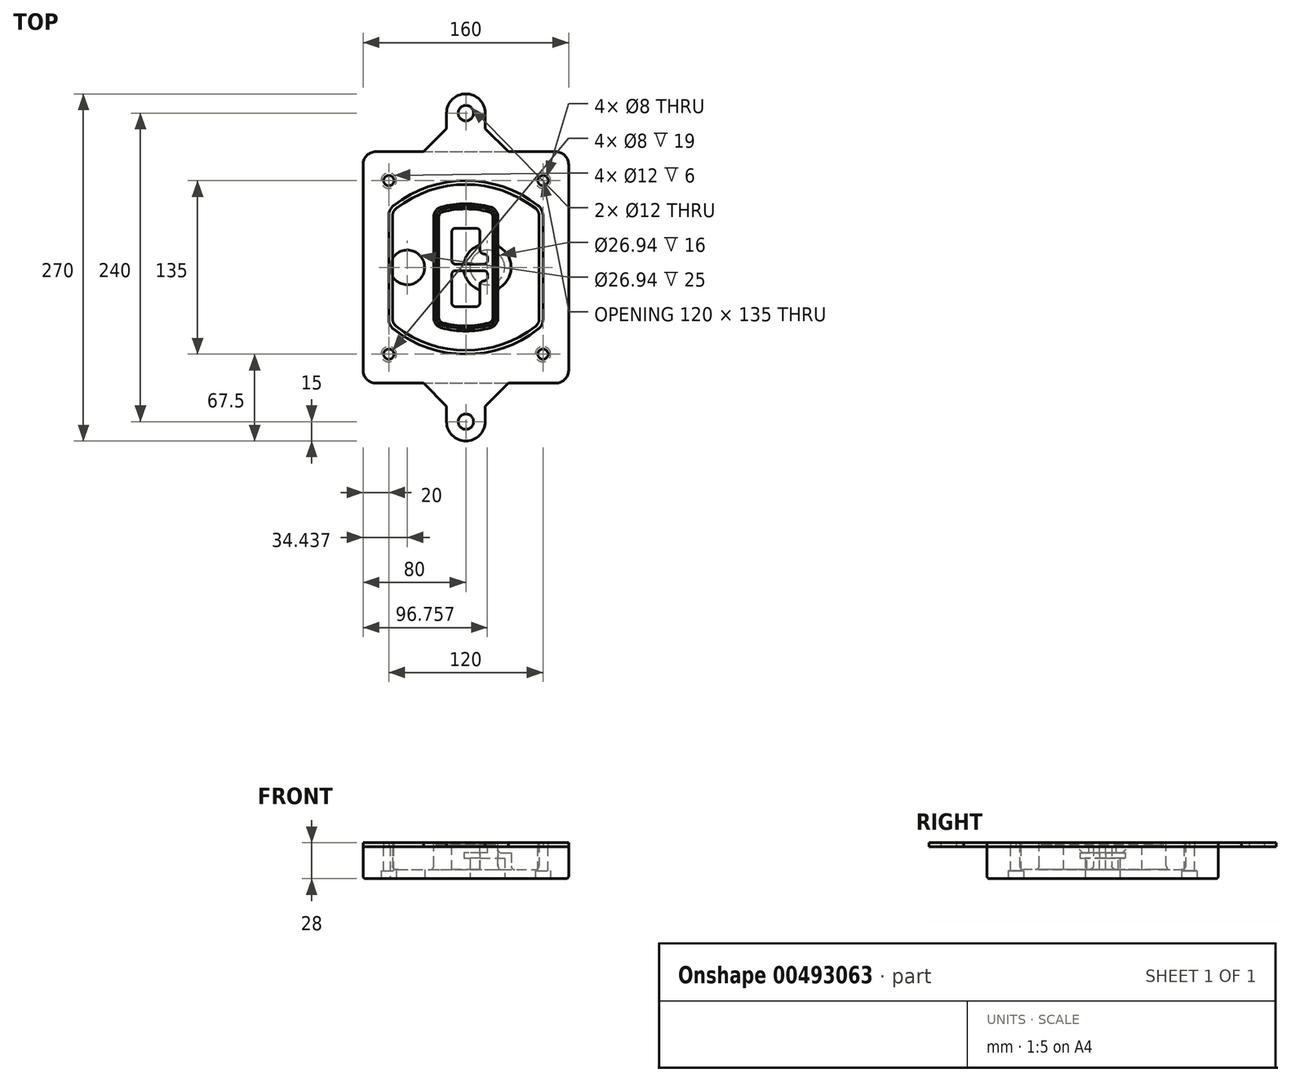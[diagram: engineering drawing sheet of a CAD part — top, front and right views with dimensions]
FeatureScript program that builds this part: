
annotation { "Feature Type Name" : "Feature", "Feature Type Description" : "" }
export const myFeature = defineFeature(function(context is Context, id is Id, definition is map)
    precondition{}
    {
        {
            var Q0;
            Q0=qCreatedBy(makeId("Top.planeOp"),FACE);
            var sketch = newSketch(context, id + "F0", { "sketchPlane" : qUnion([Q0])});
            skPoint(sketch, "E0.rect.middle", {"position": v(0, 0) * mm});
            skLineSegment(sketch, "E1.bottom", {"start": v(-70, -90) * mm, "end": v(70, -90) * mm});
            skLineSegment(sketch, "E1.top", {"start": v(-70, 90) * mm, "end": v(70, 90) * mm});
            skLineSegment(sketch, "E1.left", {"start": v(-80, -80) * mm, "end": v(-80, 80) * mm});
            skLineSegment(sketch, "E1.right", {"start": v(80, -80) * mm, "end": v(80, 80) * mm});
            skLineSegment(sketch, "E2", {"start": v(-80, 90) * mm, "end": v(80, -90) * mm, "construction": true});
            skLineSegment(sketch, "E3", {"start": v(80, 90) * mm, "end": v(-80, -90) * mm, "construction": true});
            skCircle(sketch, "E4", {"center": v(-60, 67.5) * mm, "radius": 4 * mm});
            skCircle(sketch, "E5", {"center": v(60, 67.5) * mm, "radius": 4 * mm});
            skCircle(sketch, "E6", {"center": v(60, -67.5) * mm, "radius": 4 * mm});
            skCircle(sketch, "E7", {"center": v(-60, -67.5) * mm, "radius": 4 * mm});
            skLineSegment(sketch, "E8", {"start": v(-60, 67.5) * mm, "end": v(60, 67.5) * mm, "construction": true});
            skLineSegment(sketch, "E9", {"start": v(60, 67.5) * mm, "end": v(60, -67.5) * mm, "construction": true});
            skLineSegment(sketch, "E10", {"start": v(60, -67.5) * mm, "end": v(-60, -67.5) * mm, "construction": true});
            skLineSegment(sketch, "E11", {"start": v(-60, -67.5) * mm, "end": v(-60, 67.5) * mm, "construction": true});
            skLineSegment(sketch, "E12", {"start": v(-60, 40.3) * mm, "end": v(-60, -40.3) * mm});
            skLineSegment(sketch, "E13", {"start": v(60, 40.3) * mm, "end": v(60, -40.3) * mm});
            skArc(sketch, "E14", {"start": v(56.15, 48.18) * mm, "mid": v(0, 67.5) * mm, "end": v(-56.15, 48.18) * mm});
            skArc(sketch, "E15", {"start": v(-56.15, -48.18) * mm, "mid": v(0, -67.5) * mm, "end": v(56.15, -48.18) * mm});
            skLineSegment(sketch, "E16", {"start": v(-60, 0) * mm, "end": v(60, 0) * mm, "construction": true});
            skPoint(sketch, "E17.visualSharp", {"position": v(-60, -45) * mm});
            skArc(sketch, "E17.filletArc", {"start": v(-60, -40.3) * mm, "mid": v(-58.99, -44.68) * mm, "end": v(-56.15, -48.18) * mm});
            skPoint(sketch, "E18.visualSharp", {"position": v(-60, 45) * mm});
            skArc(sketch, "E18.filletArc", {"start": v(-56.15, 48.18) * mm, "mid": v(-58.99, 44.68) * mm, "end": v(-60, 40.3) * mm});
            skPoint(sketch, "E19.visualSharp", {"position": v(60, 45) * mm});
            skArc(sketch, "E19.filletArc", {"start": v(60, 40.3) * mm, "mid": v(58.99, 44.68) * mm, "end": v(56.15, 48.18) * mm});
            skPoint(sketch, "E20.visualSharp", {"position": v(60, -45) * mm});
            skArc(sketch, "E20.filletArc", {"start": v(56.15, -48.18) * mm, "mid": v(58.99, -44.68) * mm, "end": v(60, -40.3) * mm});
            skPoint(sketch, "E21.visualSharp", {"position": v(-80, 90) * mm});
            skArc(sketch, "E21.filletArc", {"start": v(-70, 90) * mm, "mid": v(-77.07, 87.07) * mm, "end": v(-80, 80) * mm});
            skPoint(sketch, "E22.visualSharp", {"position": v(80, 90) * mm});
            skArc(sketch, "E22.filletArc", {"start": v(80, 80) * mm, "mid": v(77.07, 87.07) * mm, "end": v(70, 90) * mm});
            skPoint(sketch, "E23.visualSharp", {"position": v(80, -90) * mm});
            skArc(sketch, "E23.filletArc", {"start": v(70, -90) * mm, "mid": v(77.07, -87.07) * mm, "end": v(80, -80) * mm});
            skPoint(sketch, "E24.visualSharp", {"position": v(-80, -90) * mm});
            skArc(sketch, "E24.filletArc", {"start": v(-80, -80) * mm, "mid": v(-77.07, -87.07) * mm, "end": v(-70, -90) * mm});
            skArc(sketch, "E25.0", {"start": v(57, 40.3) * mm, "mid": v(56.3, 43.36) * mm, "end": v(54.3, 45.81) * mm});
            skLineSegment(sketch, "E25.1", {"start": v(57, 40.3) * mm, "end": v(57, -40.3) * mm});
            skArc(sketch, "E25.2", {"start": v(54.3, -45.81) * mm, "mid": v(56.3, -43.36) * mm, "end": v(57, -40.3) * mm});
            skArc(sketch, "E25.3", {"start": v(-54.3, -45.81) * mm, "mid": v(0, -64.5) * mm, "end": v(54.3, -45.81) * mm});
            skArc(sketch, "E25.4", {"start": v(-57, -40.3) * mm, "mid": v(-56.3, -43.36) * mm, "end": v(-54.3, -45.81) * mm});
            skArc(sketch, "E25.5", {"start": v(54.3, 45.81) * mm, "mid": v(0, 64.5) * mm, "end": v(-54.3, 45.81) * mm});
            skLineSegment(sketch, "E25.6", {"start": v(-57, 40.3) * mm, "end": v(-57, -40.3) * mm});
            skArc(sketch, "E25.7", {"start": v(-54.3, 45.81) * mm, "mid": v(-56.3, 43.36) * mm, "end": v(-57, 40.3) * mm});
            skArc(sketch, "E26.0", {"start": v(-58.62, 51.33) * mm, "mid": v(-62.58, 46.43) * mm, "end": v(-64, 40.3) * mm});
            skArc(sketch, "E26.1", {"start": v(58.62, 51.33) * mm, "mid": v(0, 71.5) * mm, "end": v(-58.62, 51.33) * mm});
            skArc(sketch, "E26.2", {"start": v(64, 40.3) * mm, "mid": v(62.58, 46.43) * mm, "end": v(58.62, 51.33) * mm});
            skLineSegment(sketch, "E26.3", {"start": v(64, 40.3) * mm, "end": v(64, -40.3) * mm});
            skArc(sketch, "E26.4", {"start": v(58.62, -51.33) * mm, "mid": v(62.58, -46.43) * mm, "end": v(64, -40.3) * mm});
            skLineSegment(sketch, "E26.5", {"start": v(-64, 40.3) * mm, "end": v(-64, -40.3) * mm});
            skArc(sketch, "E26.6", {"start": v(-58.62, -51.33) * mm, "mid": v(0, -71.5) * mm, "end": v(58.62, -51.33) * mm});
            skArc(sketch, "E26.7", {"start": v(-64, -40.3) * mm, "mid": v(-62.58, -46.43) * mm, "end": v(-58.62, -51.33) * mm});
            skSolve(sketch);
        }
        {
            var Q0;
            Q0=makeQuery(id+"F0.imprint","IMPRINT",FACE,{"disambiguationData":[TD([[makeQuery(id+"F0.imprint","IMPRINT",EDGE,{"derivedFrom":sQuery(id+"F0.wireOp",EDGE,"E1.bottom")}),1.0]])]});
            var Q1;
            Q1=makeQuery(id+"F0.imprint","IMPRINT",FACE,{"disambiguationData":[TD([[makeQuery(id+"F0.imprint","IMPRINT",EDGE,{"derivedFrom":sQuery(id+"F0.wireOp",EDGE,"E12")}),1.0]])]});
            var Q2;
            Q2=makeQuery(id+"F0.imprint","IMPRINT",FACE,{"disambiguationData":[TD([[makeQuery(id+"F0.imprint","IMPRINT",EDGE,{"derivedFrom":sQuery(id+"F0.wireOp",EDGE,"E25.0")}),1.0]])]});
            var Q3;
            Q3=makeQuery(id+"F0.imprint","IMPRINT",FACE,{"disambiguationData":[TD([[makeQuery(id+"F0.imprint","IMPRINT",EDGE,{"derivedFrom":sQuery(id+"F0.wireOp",EDGE,"E12")}),-1.0]])]});
            extrude(context, id + "F1", {"entities" : qUnion([Q0, Q1, Q2, Q3]), "oppositeDirection" : true, "depth" : 25 * mm});
        }
        {
            var Q0;
            Q0=makeQuery(id+"F0.imprint","IMPRINT",FACE,{"disambiguationData":[TD([[makeQuery(id+"F0.imprint","IMPRINT",EDGE,{"derivedFrom":sQuery(id+"F0.wireOp",EDGE,"E12")}),1.0]])]});
            extrude(context, id + "F2", {"entities" : qUnion([Q0]), "operationType" : NewBodyOperationType.ADD, "depth" : 3 * mm});
        }
        {
            var Q0;
            Q0=makeQuery(id+"F0.imprint","IMPRINT",FACE,{"disambiguationData":[TD([[makeQuery(id+"F0.imprint","IMPRINT",EDGE,{"derivedFrom":sQuery(id+"F0.wireOp",EDGE,"E25.0")}),1.0]])]});
            extrude(context, id + "F3", {"entities" : qUnion([Q0]), "operationType" : NewBodyOperationType.REMOVE, "oppositeDirection" : true, "depth" : 18 * mm});
        }
        {
            var Q0;
            Q0=makeQuery(id+"F2.opExtrude","CAP_FACE",FACE,{"disambiguationData":[OSD([sQuery(id+"F0.wireOp",EDGE,"E12"),sQuery(id+"F0.wireOp",EDGE,"E13"),sQuery(id+"F0.wireOp",EDGE,"E14"),sQuery(id+"F0.wireOp",EDGE,"E15"),sQuery(id+"F0.wireOp",EDGE,"E17.filletArc"),sQuery(id+"F0.wireOp",EDGE,"E18.filletArc"),sQuery(id+"F0.wireOp",EDGE,"E19.filletArc"),sQuery(id+"F0.wireOp",EDGE,"E20.filletArc"),sQuery(id+"F0.wireOp",EDGE,"E25.0"),sQuery(id+"F0.wireOp",EDGE,"E25.1"),sQuery(id+"F0.wireOp",EDGE,"E25.2"),sQuery(id+"F0.wireOp",EDGE,"E25.3"),sQuery(id+"F0.wireOp",EDGE,"E25.4"),sQuery(id+"F0.wireOp",EDGE,"E25.5"),sQuery(id+"F0.wireOp",EDGE,"E25.6"),sQuery(id+"F0.wireOp",EDGE,"E25.7")])],"isStart":false});
            var sketch = newSketch(context, id + "F4", { "sketchPlane" : qUnion([Q0])});
            skArc(sketch, "E27.0", {"start": v(-19.08, -46.97) * mm, "mid": v(0, -49.5) * mm, "end": v(19.08, -46.97) * mm});
            skArc(sketch, "E28.0", {"start": v(19.08, 46.97) * mm, "mid": v(0, 49.5) * mm, "end": v(-19.08, 46.97) * mm});
            skLineSegment(sketch, "E29", {"start": v(-25, 39.25) * mm, "end": v(-25, -39.25) * mm});
            skLineSegment(sketch, "E30", {"start": v(25, 39.25) * mm, "end": v(25, -39.25) * mm});
            skLineSegment(sketch, "E31", {"start": v(-25, 45.1) * mm, "end": v(25, 45.1) * mm, "construction": true});
            skLineSegment(sketch, "E32", {"start": v(-25, -45.1) * mm, "end": v(25, -45.1) * mm, "construction": true});
            skPoint(sketch, "E33.visualSharp", {"position": v(-25, 45.1) * mm});
            skArc(sketch, "E33.filletArc", {"start": v(-19.08, 46.97) * mm, "mid": v(-23.35, 44.11) * mm, "end": v(-25, 39.25) * mm});
            skPoint(sketch, "E34.visualSharp", {"position": v(25, 45.1) * mm});
            skArc(sketch, "E34.filletArc", {"start": v(25, 39.25) * mm, "mid": v(23.35, 44.11) * mm, "end": v(19.08, 46.97) * mm});
            skPoint(sketch, "E35.visualSharp", {"position": v(25, -45.1) * mm});
            skArc(sketch, "E35.filletArc", {"start": v(19.08, -46.97) * mm, "mid": v(23.35, -44.11) * mm, "end": v(25, -39.25) * mm});
            skPoint(sketch, "E36.visualSharp", {"position": v(-25, -45.1) * mm});
            skArc(sketch, "E36.filletArc", {"start": v(-25, -39.25) * mm, "mid": v(-23.35, -44.11) * mm, "end": v(-19.08, -46.97) * mm});
            skArc(sketch, "E37.0", {"start": v(54.3, 45.81) * mm, "mid": v(0, 64.5) * mm, "end": v(-54.3, 45.81) * mm});
            skArc(sketch, "E37.1", {"start": v(-54.3, 45.81) * mm, "mid": v(-56.3, 43.36) * mm, "end": v(-57, 40.3) * mm});
            skLineSegment(sketch, "E37.2", {"start": v(-57, 40.3) * mm, "end": v(-57, -40.3) * mm});
            skArc(sketch, "E37.3", {"start": v(-57, -40.3) * mm, "mid": v(-56.3, -43.36) * mm, "end": v(-54.3, -45.81) * mm});
            skArc(sketch, "E37.4", {"start": v(-54.3, -45.81) * mm, "mid": v(0, -64.5) * mm, "end": v(54.3, -45.81) * mm});
            skArc(sketch, "E37.5", {"start": v(54.3, -45.81) * mm, "mid": v(56.3, -43.36) * mm, "end": v(57, -40.3) * mm});
            skLineSegment(sketch, "E37.6", {"start": v(57, 40.3) * mm, "end": v(57, -40.3) * mm});
            skArc(sketch, "E37.7", {"start": v(57, 40.3) * mm, "mid": v(56.3, 43.36) * mm, "end": v(54.3, 45.81) * mm});
            skLineSegment(sketch, "E38.0", {"start": v(23, 39.25) * mm, "end": v(23, -39.25) * mm});
            skArc(sketch, "E38.1", {"start": v(18.56, -45.04) * mm, "mid": v(21.76, -42.9) * mm, "end": v(23, -39.25) * mm});
            skArc(sketch, "E38.2", {"start": v(-18.56, -45.04) * mm, "mid": v(0, -47.5) * mm, "end": v(18.56, -45.04) * mm});
            skArc(sketch, "E38.3", {"start": v(-23, -39.25) * mm, "mid": v(-21.76, -42.9) * mm, "end": v(-18.56, -45.04) * mm});
            skLineSegment(sketch, "E38.4", {"start": v(-23, 39.25) * mm, "end": v(-23, -39.25) * mm});
            skArc(sketch, "E38.5", {"start": v(23, 39.25) * mm, "mid": v(21.76, 42.9) * mm, "end": v(18.56, 45.04) * mm});
            skArc(sketch, "E38.6", {"start": v(-18.56, 45.04) * mm, "mid": v(-21.76, 42.9) * mm, "end": v(-23, 39.25) * mm});
            skArc(sketch, "E38.7", {"start": v(18.56, 45.04) * mm, "mid": v(0, 47.5) * mm, "end": v(-18.56, 45.04) * mm});
            skArc(sketch, "E39.0", {"start": v(21, 39.25) * mm, "mid": v(20.18, 41.68) * mm, "end": v(18.04, 43.1) * mm});
            skLineSegment(sketch, "E39.1", {"start": v(21, 39.25) * mm, "end": v(21, -39.25) * mm});
            skArc(sketch, "E39.2", {"start": v(18.04, -43.1) * mm, "mid": v(20.18, -41.68) * mm, "end": v(21, -39.25) * mm});
            skArc(sketch, "E39.3", {"start": v(-18.04, -43.1) * mm, "mid": v(0, -45.5) * mm, "end": v(18.04, -43.1) * mm});
            skArc(sketch, "E39.4", {"start": v(-21, -39.25) * mm, "mid": v(-20.18, -41.68) * mm, "end": v(-18.04, -43.1) * mm});
            skArc(sketch, "E39.5", {"start": v(18.04, 43.1) * mm, "mid": v(0, 45.5) * mm, "end": v(-18.04, 43.1) * mm});
            skLineSegment(sketch, "E39.6", {"start": v(-21, 39.25) * mm, "end": v(-21, -39.25) * mm});
            skArc(sketch, "E39.7", {"start": v(-18.04, 43.1) * mm, "mid": v(-20.18, 41.68) * mm, "end": v(-21, 39.25) * mm});
            skLineSegment(sketch, "E40", {"start": v(-25, 0) * mm, "end": v(25, 0) * mm, "construction": true});
            skLineSegment(sketch, "E41", {"start": v(-11, 5.5) * mm, "end": v(-11, 27.5) * mm});
            skLineSegment(sketch, "E42", {"start": v(-8, 30.5) * mm, "end": v(8, 30.5) * mm});
            skLineSegment(sketch, "E43", {"start": v(11, 27.5) * mm, "end": v(11, 13.5) * mm});
            skLineSegment(sketch, "E44", {"start": v(14, 10.5) * mm, "end": v(14, 10.5) * mm});
            skLineSegment(sketch, "E45", {"start": v(17, 7.5) * mm, "end": v(17, 5.5) * mm});
            skLineSegment(sketch, "E46", {"start": v(14, 2.5) * mm, "end": v(-8, 2.5) * mm});
            skPoint(sketch, "E47.visualSharp", {"position": v(-11, 30.5) * mm});
            skArc(sketch, "E47.filletArc", {"start": v(-8, 30.5) * mm, "mid": v(-10.12, 29.62) * mm, "end": v(-11, 27.5) * mm});
            skPoint(sketch, "E48.visualSharp", {"position": v(11, 30.5) * mm});
            skArc(sketch, "E48.filletArc", {"start": v(11, 27.5) * mm, "mid": v(10.12, 29.62) * mm, "end": v(8, 30.5) * mm});
            skPoint(sketch, "E49.visualSharp", {"position": v(11, 10.5) * mm});
            skArc(sketch, "E49.filletArc", {"start": v(11, 13.5) * mm, "mid": v(11.88, 11.38) * mm, "end": v(14, 10.5) * mm});
            skPoint(sketch, "E50.visualSharp", {"position": v(17, 10.5) * mm});
            skArc(sketch, "E50.filletArc", {"start": v(17, 7.5) * mm, "mid": v(16.12, 9.62) * mm, "end": v(14, 10.5) * mm});
            skPoint(sketch, "E51.visualSharp", {"position": v(17, 2.5) * mm});
            skArc(sketch, "E51.filletArc", {"start": v(14, 2.5) * mm, "mid": v(16.12, 3.38) * mm, "end": v(17, 5.5) * mm});
            skPoint(sketch, "E52.visualSharp", {"position": v(-11, 2.5) * mm});
            skArc(sketch, "E52.filletArc", {"start": v(-11, 5.5) * mm, "mid": v(-10.12, 3.38) * mm, "end": v(-8, 2.5) * mm});
            skLineSegment(sketch, "E53.0.MirrorCS", {"start": v(14, -2.5) * mm, "end": v(-8, -2.5) * mm});
            skArc(sketch, "E54.0.MirrorCS", {"start": v(-11, -5.5) * mm, "mid": v(-10.12, -3.38) * mm, "end": v(-8, -2.5) * mm});
            skLineSegment(sketch, "E55.0.MirrorCS", {"start": v(-11, -5.5) * mm, "end": v(-11, -27.5) * mm});
            skArc(sketch, "E56.0.MirrorCS", {"start": v(-8, -30.5) * mm, "mid": v(-10.12, -29.62) * mm, "end": v(-11, -27.5) * mm});
            skLineSegment(sketch, "E57.0.MirrorCS", {"start": v(-8, -30.5) * mm, "end": v(8, -30.5) * mm});
            skArc(sketch, "E58.0.MirrorCS", {"start": v(11, -27.5) * mm, "mid": v(10.12, -29.62) * mm, "end": v(8, -30.5) * mm});
            skLineSegment(sketch, "E59.0.MirrorCS", {"start": v(11, -27.5) * mm, "end": v(11, -13.5) * mm});
            skArc(sketch, "E60.0.MirrorCS", {"start": v(11, -13.5) * mm, "mid": v(11.88, -11.38) * mm, "end": v(14, -10.5) * mm});
            skArc(sketch, "E61.0.MirrorCS", {"start": v(17, -7.5) * mm, "mid": v(16.12, -9.62) * mm, "end": v(14, -10.5) * mm});
            skLineSegment(sketch, "E62.0.MirrorCS", {"start": v(17, -7.5) * mm, "end": v(17, -5.5) * mm});
            skArc(sketch, "E63.0.MirrorCS", {"start": v(14, -2.5) * mm, "mid": v(16.12, -3.38) * mm, "end": v(17, -5.5) * mm});
            skSolve(sketch);
        }
        {
            var Q0;
            Q0=makeQuery(id+"F4.imprint","IMPRINT",FACE,{"disambiguationData":[TD([[makeQuery(id+"F4.imprint","IMPRINT",EDGE,{"derivedFrom":sQuery(id+"F4.wireOp",EDGE,"E27.0")}),1.0]])]});
            var Q1;
            Q1=makeQuery(id+"F4.imprint","IMPRINT",FACE,{"disambiguationData":[TD([[makeQuery(id+"F4.imprint","IMPRINT",EDGE,{"derivedFrom":sQuery(id+"F4.wireOp",EDGE,"E38.0")}),-1.0]])]});
            var Q2;
            Q2=makeQuery(id+"F4.imprint","IMPRINT",FACE,{"disambiguationData":[TD([[makeQuery(id+"F4.imprint","IMPRINT",EDGE,{"derivedFrom":sQuery(id+"F4.wireOp",EDGE,"E39.0")}),1.0]])]});
            extrude(context, id + "F5", {"entities" : qUnion([Q0, Q1, Q2]), "operationType" : NewBodyOperationType.ADD, "endBound" : BoundingType.UP_TO_NEXT, "oppositeDirection" : true, "depth" : 25 * mm});
        }
        {
            var Q0;
            Q0=makeQuery(id+"F4.imprint","IMPRINT",FACE,{"disambiguationData":[TD([[makeQuery(id+"F4.imprint","IMPRINT",EDGE,{"derivedFrom":sQuery(id+"F4.wireOp",EDGE,"E38.0")}),-1.0]])]});
            extrude(context, id + "F6", {"entities" : qUnion([Q0]), "operationType" : NewBodyOperationType.REMOVE, "oppositeDirection" : true, "depth" : 2 * mm});
        }
        {
            var Q0;
            Q0=makeQuery(id+"F1.opExtrude","CAP_FACE",FACE,{"disambiguationData":[OSD([sQuery(id+"F0.wireOp",EDGE,"E1.bottom"),sQuery(id+"F0.wireOp",EDGE,"E1.top"),sQuery(id+"F0.wireOp",EDGE,"E1.left"),sQuery(id+"F0.wireOp",EDGE,"E1.right"),sQuery(id+"F0.wireOp",EDGE,"E4"),sQuery(id+"F0.wireOp",EDGE,"E5"),sQuery(id+"F0.wireOp",EDGE,"E6"),sQuery(id+"F0.wireOp",EDGE,"E7"),sQuery(id+"F0.wireOp",EDGE,"E21.filletArc"),sQuery(id+"F0.wireOp",EDGE,"E22.filletArc"),sQuery(id+"F0.wireOp",EDGE,"E23.filletArc"),sQuery(id+"F0.wireOp",EDGE,"E24.filletArc")])],"isStart":false});
            var sketch = newSketch(context, id + "F7", { "sketchPlane" : qUnion([Q0])});
            skCircle(sketch, "E64", {"center": v(16.76, 0) * mm, "radius": 13.47 * mm});
            skCircle(sketch, "E65", {"center": v(-45.56, 0) * mm, "radius": 13.47 * mm});
            skLineSegment(sketch, "E66", {"start": v(80, 0) * mm, "end": v(-80, 0) * mm});
            skCircle(sketch, "E67", {"center": v(16.76, 0) * mm, "radius": 18.47 * mm});
            skCircle(sketch, "E68", {"center": v(60, -67.5) * mm, "radius": 6 * mm});
            skCircle(sketch, "E69", {"center": v(-60, -67.5) * mm, "radius": 6 * mm});
            skCircle(sketch, "E70", {"center": v(-60, 67.5) * mm, "radius": 6 * mm});
            skCircle(sketch, "E71", {"center": v(60, 67.5) * mm, "radius": 6 * mm});
            skSolve(sketch);
        }
        {
            var Q0;
            {var subQ1=sQuery(id+"F7.wireOp",EDGE,"E66");var subQ4=sQuery(id+"F7.wireOp",EDGE,"E64");var subQ6=makeQuery(id+"F7.imprint","INTERSECT",VERTEX,{"disambiguationData":[OD(0.0)],"derivedFrom":[subQ4,subQ1]});Q0=makeQuery(id+"F7.imprint","IMPRINT",FACE,{"disambiguationData":[TD([[makeQuery(id+"F7.imprint","IMPRINT",EDGE,{"disambiguationData":[TD([[subQ6,-1.0]])],"derivedFrom":subQ4}),-1.0]])]});}
            var Q1;
            {var subQ0=sQuery(id+"F7.wireOp",EDGE,"E66");var subQ1=sQuery(id+"F7.wireOp",EDGE,"E64");var subQ3=makeQuery(id+"F7.imprint","INTERSECT",VERTEX,{"disambiguationData":[OD(0.0)],"derivedFrom":[subQ1,subQ0]});Q1=makeQuery(id+"F7.imprint","IMPRINT",FACE,{"disambiguationData":[TD([[makeQuery(id+"F7.imprint","IMPRINT",EDGE,{"disambiguationData":[TD([[subQ3,-1.0]])],"derivedFrom":subQ1}),1.0]])]});}
            var Q2;
            {var subQ0=sQuery(id+"F7.wireOp",EDGE,"E66");var subQ1=sQuery(id+"F7.wireOp",EDGE,"E64");var subQ3=makeQuery(id+"F7.imprint","INTERSECT",VERTEX,{"disambiguationData":[OD(0.0)],"derivedFrom":[subQ1,subQ0]});Q2=makeQuery(id+"F7.imprint","IMPRINT",FACE,{"disambiguationData":[TD([[makeQuery(id+"F7.imprint","IMPRINT",EDGE,{"disambiguationData":[TD([[subQ3,1.0]])],"derivedFrom":subQ1}),1.0]])]});}
            var Q3;
            {var subQ1=sQuery(id+"F7.wireOp",EDGE,"E66");var subQ4=sQuery(id+"F7.wireOp",EDGE,"E64");var subQ6=makeQuery(id+"F7.imprint","INTERSECT",VERTEX,{"disambiguationData":[OD(0.0)],"derivedFrom":[subQ4,subQ1]});Q3=makeQuery(id+"F7.imprint","IMPRINT",FACE,{"disambiguationData":[TD([[makeQuery(id+"F7.imprint","IMPRINT",EDGE,{"disambiguationData":[TD([[subQ6,1.0]])],"derivedFrom":subQ4}),-1.0]])]});}
            extrude(context, id + "F8", {"entities" : qUnion([Q0, Q1, Q2, Q3]), "operationType" : NewBodyOperationType.ADD, "oppositeDirection" : true, "depth" : 20 * mm});
        }
        {
            var Q0;
            {var subQ0=sQuery(id+"F7.wireOp",EDGE,"E66");var subQ1=sQuery(id+"F7.wireOp",EDGE,"E64");var subQ3=makeQuery(id+"F7.imprint","INTERSECT",VERTEX,{"disambiguationData":[OD(0.0)],"derivedFrom":[subQ1,subQ0]});Q0=makeQuery(id+"F7.imprint","IMPRINT",FACE,{"disambiguationData":[TD([[makeQuery(id+"F7.imprint","IMPRINT",EDGE,{"disambiguationData":[TD([[subQ3,-1.0]])],"derivedFrom":subQ1}),1.0]])]});}
            var Q1;
            {var subQ0=sQuery(id+"F7.wireOp",EDGE,"E66");var subQ1=sQuery(id+"F7.wireOp",EDGE,"E64");var subQ3=makeQuery(id+"F7.imprint","INTERSECT",VERTEX,{"disambiguationData":[OD(0.0)],"derivedFrom":[subQ1,subQ0]});Q1=makeQuery(id+"F7.imprint","IMPRINT",FACE,{"disambiguationData":[TD([[makeQuery(id+"F7.imprint","IMPRINT",EDGE,{"disambiguationData":[TD([[subQ3,1.0]])],"derivedFrom":subQ1}),1.0]])]});}
            extrude(context, id + "F9", {"entities" : qUnion([Q0, Q1]), "operationType" : NewBodyOperationType.REMOVE, "oppositeDirection" : true, "depth" : 16 * mm});
        }
        {
            var Q0;
            {var subQ0=sQuery(id+"F7.wireOp",EDGE,"E66");var subQ1=sQuery(id+"F7.wireOp",EDGE,"E65");var subQ3=makeQuery(id+"F7.imprint","INTERSECT",VERTEX,{"disambiguationData":[OD(0.0)],"derivedFrom":[subQ1,subQ0]});Q0=makeQuery(id+"F7.imprint","IMPRINT",FACE,{"disambiguationData":[TD([[makeQuery(id+"F7.imprint","IMPRINT",EDGE,{"disambiguationData":[TD([[subQ3,-1.0]])],"derivedFrom":subQ1}),1.0]])]});}
            var Q1;
            {var subQ0=sQuery(id+"F7.wireOp",EDGE,"E66");var subQ1=sQuery(id+"F7.wireOp",EDGE,"E65");var subQ3=makeQuery(id+"F7.imprint","INTERSECT",VERTEX,{"disambiguationData":[OD(0.0)],"derivedFrom":[subQ1,subQ0]});Q1=makeQuery(id+"F7.imprint","IMPRINT",FACE,{"disambiguationData":[TD([[makeQuery(id+"F7.imprint","IMPRINT",EDGE,{"disambiguationData":[TD([[subQ3,1.0]])],"derivedFrom":subQ1}),1.0]])]});}
            extrude(context, id + "F10", {"entities" : qUnion([Q0, Q1]), "operationType" : NewBodyOperationType.REMOVE, "oppositeDirection" : true, "depth" : 25 * mm});
        }
        {
            var Q0;
            Q0=makeQuery(id+"F7.imprint","IMPRINT",FACE,{"disambiguationData":[TD([[makeQuery(id+"F7.imprint","IMPRINT",EDGE,{"derivedFrom":sQuery(id+"F7.wireOp",EDGE,"E68")}),1.0]])]});
            var Q1;
            Q1=makeQuery(id+"F7.imprint","IMPRINT",FACE,{"disambiguationData":[TD([[makeQuery(id+"F7.imprint","IMPRINT",EDGE,{"derivedFrom":makeQuery(id+"F1.opExtrude","CAP_EDGE",EDGE,{"disambiguationData":[OSD([sQuery(id+"F0.wireOp",EDGE,"E5")])],"isStart":false})}),-1.0]])]});
            var Q2;
            Q2=makeQuery(id+"F7.imprint","IMPRINT",FACE,{"disambiguationData":[TD([[makeQuery(id+"F7.imprint","IMPRINT",EDGE,{"derivedFrom":sQuery(id+"F7.wireOp",EDGE,"E69")}),1.0]])]});
            var Q3;
            Q3=makeQuery(id+"F7.imprint","IMPRINT",FACE,{"disambiguationData":[TD([[makeQuery(id+"F7.imprint","IMPRINT",EDGE,{"derivedFrom":makeQuery(id+"F1.opExtrude","CAP_EDGE",EDGE,{"disambiguationData":[OSD([sQuery(id+"F0.wireOp",EDGE,"E4")])],"isStart":false})}),-1.0]])]});
            var Q4;
            Q4=makeQuery(id+"F7.imprint","IMPRINT",FACE,{"disambiguationData":[TD([[makeQuery(id+"F7.imprint","IMPRINT",EDGE,{"derivedFrom":sQuery(id+"F7.wireOp",EDGE,"E70")}),1.0]])]});
            var Q5;
            Q5=makeQuery(id+"F7.imprint","IMPRINT",FACE,{"disambiguationData":[TD([[makeQuery(id+"F7.imprint","IMPRINT",EDGE,{"derivedFrom":makeQuery(id+"F1.opExtrude","CAP_EDGE",EDGE,{"disambiguationData":[OSD([sQuery(id+"F0.wireOp",EDGE,"E7")])],"isStart":false})}),-1.0]])]});
            var Q6;
            Q6=makeQuery(id+"F7.imprint","IMPRINT",FACE,{"disambiguationData":[TD([[makeQuery(id+"F7.imprint","IMPRINT",EDGE,{"derivedFrom":sQuery(id+"F7.wireOp",EDGE,"E71")}),1.0]])]});
            var Q7;
            Q7=makeQuery(id+"F7.imprint","IMPRINT",FACE,{"disambiguationData":[TD([[makeQuery(id+"F7.imprint","IMPRINT",EDGE,{"derivedFrom":makeQuery(id+"F1.opExtrude","CAP_EDGE",EDGE,{"disambiguationData":[OSD([sQuery(id+"F0.wireOp",EDGE,"E6")])],"isStart":false})}),-1.0]])]});
            extrude(context, id + "F11", {"entities" : qUnion([Q0, Q1, Q2, Q3, Q4, Q5, Q6, Q7]), "operationType" : NewBodyOperationType.REMOVE, "oppositeDirection" : true, "depth" : 6 * mm});
        }
        {
            var Q0;
            Q0=makeQuery(id+"F9.boolean.opBoolean","COPY",FACE,{"derivedFrom":makeQuery(id+"F9.opExtrude","CAP_FACE",FACE,{"disambiguationData":[OSD([sQuery(id+"F7.wireOp",EDGE,"E64")])],"isStart":false})});
            var sketch = newSketch(context, id + "F12", { "sketchPlane" : qUnion([Q0])});
            skArc(sketch, "E72.0", {"start": v(11, 17.55) * mm, "mid": v(2.57, 11.82) * mm, "end": v(-1.54, 2.5) * mm});
            skArc(sketch, "E72.1", {"start": v(-1.54, -2.5) * mm, "mid": v(2.57, -11.82) * mm, "end": v(11, -17.55) * mm});
            skLineSegment(sketch, "E73", {"start": v(-1.54, -2.5) * mm, "end": v(14, -2.5) * mm});
            skLineSegment(sketch, "E74.0", {"start": v(14, 2.5) * mm, "end": v(-1.54, 2.5) * mm});
            skArc(sketch, "E74.1", {"start": v(14, 2.5) * mm, "mid": v(16.12, 3.38) * mm, "end": v(17, 5.5) * mm});
            skLineSegment(sketch, "E74.2", {"start": v(17, 7.5) * mm, "end": v(17, 5.5) * mm});
            skArc(sketch, "E74.3", {"start": v(17, 7.5) * mm, "mid": v(16.12, 9.62) * mm, "end": v(14, 10.5) * mm});
            skArc(sketch, "E74.4", {"start": v(11, 13.5) * mm, "mid": v(11.88, 11.38) * mm, "end": v(14, 10.5) * mm});
            skLineSegment(sketch, "E74.5", {"start": v(11, 17.55) * mm, "end": v(11, 13.5) * mm});
            skLineSegment(sketch, "E74.7", {"start": v(14, -2.5) * mm, "end": v(-1.54, -2.5) * mm});
            skArc(sketch, "E74.8", {"start": v(14, -2.5) * mm, "mid": v(16.12, -3.38) * mm, "end": v(17, -5.5) * mm});
            skLineSegment(sketch, "E74.9", {"start": v(17, -7.5) * mm, "end": v(17, -5.5) * mm});
            skArc(sketch, "E74.10", {"start": v(17, -7.5) * mm, "mid": v(16.12, -9.62) * mm, "end": v(14, -10.5) * mm});
            skArc(sketch, "E74.11", {"start": v(11, -13.5) * mm, "mid": v(11.88, -11.38) * mm, "end": v(14, -10.5) * mm});
            skLineSegment(sketch, "E74.12", {"start": v(11, -17.55) * mm, "end": v(11, -13.5) * mm});
            skPoint(sketch, "E75.orphan", {"position": v(11, -27.5) * mm});
            skPoint(sketch, "E76.orphan", {"position": v(-8, -2.5) * mm});
            skPoint(sketch, "E77.orphan", {"position": v(-8, 2.5) * mm});
            skPoint(sketch, "E78.orphan", {"position": v(11, 27.5) * mm});
            skSolve(sketch);
        }
        {
            var Q0;
            {var subQ7=sQuery(id+"F12.wireOp",EDGE,"E72.0");var subQ14=sQuery(id+"F12.wireOp",EDGE,"E72.1");var subQ16=sQuery(id+"F12.wireOp",EDGE,"E74.1");var subQ18=sQuery(id+"F12.wireOp",EDGE,"E74.8");Q0=qUnion([makeQuery(id+"F12.imprint","IMPRINT",FACE,{"disambiguationData":[TD([[makeQuery(id+"F12.imprint","IMPRINT",EDGE,{"derivedFrom":subQ7}),1.0]])]}),makeQuery(id+"F12.imprint","IMPRINT",FACE,{"disambiguationData":[TD([[makeQuery(id+"F12.imprint","IMPRINT",EDGE,{"derivedFrom":subQ14}),1.0]])]}),makeQuery(id+"F12.imprint","IMPRINT",FACE,{"disambiguationData":[TD([[makeQuery(id+"F12.imprint","IMPRINT",EDGE,{"derivedFrom":subQ16}),1.0]])]}),makeQuery(id+"F12.imprint","IMPRINT",FACE,{"disambiguationData":[TD([[makeQuery(id+"F12.imprint","IMPRINT",EDGE,{"derivedFrom":subQ18}),-1.0]])]})]);}
            var Q1;
            Q1=makeQuery(id+"F5.boolean.opBoolean","SPLIT",FACE,{"disambiguationData":[TD([makeQuery(id+"F5.opExtrude","SWEPT_FACE",FACE,{"disambiguationData":[OSD([sQuery(id+"F4.wireOp",EDGE,"E41")])]})])],"derivedFrom":makeQuery(id+"F3.boolean.opBoolean","COPY",FACE,{"derivedFrom":makeQuery(id+"F3.opExtrude","CAP_FACE",FACE,{"disambiguationData":[OSD([sQuery(id+"F0.wireOp",EDGE,"E25.0"),sQuery(id+"F0.wireOp",EDGE,"E25.1"),sQuery(id+"F0.wireOp",EDGE,"E25.2"),sQuery(id+"F0.wireOp",EDGE,"E25.3"),sQuery(id+"F0.wireOp",EDGE,"E25.4"),sQuery(id+"F0.wireOp",EDGE,"E25.5"),sQuery(id+"F0.wireOp",EDGE,"E25.6"),sQuery(id+"F0.wireOp",EDGE,"E25.7")])],"isStart":false})})});
            extrude(context, id + "F13", {"entities" : qUnion([Q0]), "operationType" : NewBodyOperationType.REMOVE, "endBound" : BoundingType.UP_TO_SURFACE, "endBoundEntityFace" : qUnion([Q1]), "depth" : 25 * mm});
        }
        {
            var Q0;
            Q0=makeQuery(id+"F3.boolean.opBoolean","COPY",EDGE,{"derivedFrom":makeQuery(id+"F3.opExtrude","CAP_EDGE",EDGE,{"disambiguationData":[OSD([sQuery(id+"F0.wireOp",EDGE,"E25.6")])],"isStart":false})});
            var Q1;
            Q1=makeQuery(id+"F8.boolean.opBoolean","INTERSECT",EDGE,{"derivedFrom":[makeQuery(id+"F5.opExtrude","SWEPT_FACE",FACE,{"disambiguationData":[OSD([sQuery(id+"F4.wireOp",EDGE,"E30")])]}),makeQuery(id+"F8.opExtrude","CAP_FACE",FACE,{"disambiguationData":[OSD([sQuery(id+"F7.wireOp",EDGE,"E67")])],"isStart":false})]});
            var Q2;
            Q2=makeQuery(id+"F8.boolean.opBoolean","INTERSECT",EDGE,{"disambiguationData":[OD(1.0)],"derivedFrom":[makeQuery(id+"F5.opExtrude","SWEPT_FACE",FACE,{"disambiguationData":[OSD([sQuery(id+"F4.wireOp",EDGE,"E30")])]}),makeQuery(id+"F8.opExtrude","SWEPT_FACE",FACE,{"disambiguationData":[OSD([sQuery(id+"F7.wireOp",EDGE,"E67")])]})]});
            var Q3;
            {var subQ0=sQuery(id+"F4.wireOp",EDGE,"E30");Q3=makeQuery(id+"F8.boolean.opBoolean","SPLIT",EDGE,{"disambiguationData":[TD([makeQuery(id+"F5.opExtrude","SWEPT_FACE",FACE,{"disambiguationData":[OSD([sQuery(id+"F4.wireOp",EDGE,"E35.filletArc")])]})])],"derivedFrom":makeQuery(id+"F5.opExtrude","CAP_EDGE",EDGE,{"disambiguationData":[OSD([subQ0])],"isStart":false})});}
            var Q4;
            {var subQ0=sQuery(id+"F0.wireOp",EDGE,"E25.7");var subQ1=sQuery(id+"F0.wireOp",EDGE,"E25.1");var subQ2=sQuery(id+"F0.wireOp",EDGE,"E25.6");var subQ3=sQuery(id+"F0.wireOp",EDGE,"E25.5");var subQ4=sQuery(id+"F0.wireOp",EDGE,"E25.4");var subQ5=sQuery(id+"F0.wireOp",EDGE,"E25.0");var subQ6=sQuery(id+"F0.wireOp",EDGE,"E25.2");var subQ7=sQuery(id+"F0.wireOp",EDGE,"E25.3");Q4=makeQuery(id+"F8.boolean.opBoolean","INTERSECT",EDGE,{"derivedFrom":[makeQuery(id+"F5.boolean.opBoolean","SPLIT",FACE,{"disambiguationData":[TD([makeQuery(id+"F2.opExtrude","SWEPT_FACE",FACE,{"disambiguationData":[OSD([subQ5])]})])],"derivedFrom":makeQuery(id+"F3.boolean.opBoolean","COPY",FACE,{"derivedFrom":makeQuery(id+"F3.opExtrude","CAP_FACE",FACE,{"disambiguationData":[OSD([subQ5,subQ1,subQ6,subQ7,subQ4,subQ3,subQ2,subQ0])],"isStart":false})})}),makeQuery(id+"F8.opExtrude","SWEPT_FACE",FACE,{"disambiguationData":[OSD([sQuery(id+"F7.wireOp",EDGE,"E67")])]})]});}
            var Q5;
            Q5=makeQuery(id+"F8.boolean.opBoolean","INTERSECT",EDGE,{"disambiguationData":[OD(0.0)],"derivedFrom":[makeQuery(id+"F5.opExtrude","SWEPT_FACE",FACE,{"disambiguationData":[OSD([sQuery(id+"F4.wireOp",EDGE,"E30")])]}),makeQuery(id+"F8.opExtrude","SWEPT_FACE",FACE,{"disambiguationData":[OSD([sQuery(id+"F7.wireOp",EDGE,"E67")])]})]});
            fillet(context, id + "F14", {"entities" : qUnion([Q0, Q1, Q2, Q3, Q4, Q5]), "radius" : 3 * mm, "tangentPropagation" : true, "allowEdgeOverflow" : false});
        }
        {
            var Q0;
            Q0=makeQuery(id+"F1.opExtrude","CAP_EDGE",EDGE,{"disambiguationData":[OSD([sQuery(id+"F0.wireOp",EDGE,"E1.bottom")])],"isStart":false});
            fillet(context, id + "F15", {"entities" : qUnion([Q0]), "radius" : 2 * mm, "tangentPropagation" : true, "allowEdgeOverflow" : false});
        }
        {
            var Q0;
            {var subQ0=sQuery(id+"F0.wireOp",EDGE,"E21.filletArc");var subQ1=sQuery(id+"F0.wireOp",EDGE,"E7");var subQ2=sQuery(id+"F0.wireOp",EDGE,"E6");var subQ3=sQuery(id+"F0.wireOp",EDGE,"E5");var subQ4=sQuery(id+"F0.wireOp",EDGE,"E4");var subQ5=sQuery(id+"F0.wireOp",EDGE,"E22.filletArc");var subQ6=sQuery(id+"F0.wireOp",EDGE,"E1.bottom");var subQ7=sQuery(id+"F0.wireOp",EDGE,"E1.right");var subQ8=sQuery(id+"F0.wireOp",EDGE,"E1.top");var subQ9=sQuery(id+"F0.wireOp",EDGE,"E1.left");var subQ10=sQuery(id+"F0.wireOp",EDGE,"E23.filletArc");var subQ11=sQuery(id+"F0.wireOp",EDGE,"E24.filletArc");Q0=makeQuery(id+"F2.boolean.opBoolean","SPLIT",FACE,{"disambiguationData":[TD([makeQuery(id+"F1.opExtrude","SWEPT_FACE",FACE,{"disambiguationData":[OSD([subQ6])]})])],"derivedFrom":makeQuery(id+"F1.opExtrude","CAP_FACE",FACE,{"disambiguationData":[OSD([subQ6,subQ8,subQ9,subQ7,subQ4,subQ3,subQ2,subQ1,subQ0,subQ5,subQ10,subQ11])],"isStart":true})});}
            var sketch = newSketch(context, id + "F16", { "sketchPlane" : qUnion([Q0])});
            skLineSegment(sketch, "E79.0", {"start": v(-70, 90) * mm, "end": v(70, 90) * mm});
            skArc(sketch, "E80.0", {"start": v(-70, 90) * mm, "mid": v(-77.07, 87.07) * mm, "end": v(-80, 80) * mm});
            skLineSegment(sketch, "E81.0", {"start": v(-80, -80) * mm, "end": v(-80, 80) * mm});
            skPoint(sketch, "E82.0", {"position": v(-77.07, -87.07) * mm});
            skLineSegment(sketch, "E83.0", {"start": v(-70, -90) * mm, "end": v(70, -90) * mm});
            skArc(sketch, "E84.0", {"start": v(-80, -80) * mm, "mid": v(-77.07, -87.07) * mm, "end": v(-70, -90) * mm});
            skPoint(sketch, "E85.0", {"position": v(77.07, -87.07) * mm});
            skArc(sketch, "E86.0", {"start": v(70, -90) * mm, "mid": v(77.07, -87.07) * mm, "end": v(80, -80) * mm});
            skLineSegment(sketch, "E87.0.0", {"start": v(70, 90) * mm, "end": v(-70, 90) * mm});
            skLineSegment(sketch, "E87.0.2", {"start": v(-80, 80) * mm, "end": v(-80, -80) * mm});
            skLineSegment(sketch, "E87.0.6", {"start": v(80, -80) * mm, "end": v(80, 80) * mm});
            skArc(sketch, "E87.0.7", {"start": v(80, 80) * mm, "mid": v(77.07, 87.07) * mm, "end": v(70, 90) * mm});
            skCircle(sketch, "E88.0", {"center": v(60, 67.5) * mm, "radius": 4 * mm});
            skCircle(sketch, "E89.0", {"center": v(60, -67.5) * mm, "radius": 4 * mm});
            skCircle(sketch, "E90.0", {"center": v(-60, -67.5) * mm, "radius": 4 * mm});
            skCircle(sketch, "E91.0", {"center": v(-60, 67.5) * mm, "radius": 4 * mm});
            skArc(sketch, "E92.0", {"start": v(56.15, 48.18) * mm, "mid": v(0, 67.5) * mm, "end": v(-56.15, 48.18) * mm});
            skPoint(sketch, "E93.0", {"position": v(-58.99, 44.68) * mm});
            skLineSegment(sketch, "E94.0", {"start": v(-60, 40.3) * mm, "end": v(-60, -40.3) * mm});
            skArc(sketch, "E95.0", {"start": v(-56.15, -48.18) * mm, "mid": v(0, -67.5) * mm, "end": v(56.15, -48.18) * mm});
            skLineSegment(sketch, "E96.0", {"start": v(60, 40.3) * mm, "end": v(60, -40.3) * mm});
            skArc(sketch, "E97.0", {"start": v(56.15, -48.18) * mm, "mid": v(58.99, -44.68) * mm, "end": v(60, -40.3) * mm});
            skPoint(sketch, "E98.0", {"position": v(-58.99, -44.68) * mm});
            skArc(sketch, "E99.0", {"start": v(-60, -40.3) * mm, "mid": v(-58.99, -44.68) * mm, "end": v(-56.15, -48.18) * mm});
            skArc(sketch, "E100.0", {"start": v(-56.15, 48.18) * mm, "mid": v(-58.99, 44.68) * mm, "end": v(-60, 40.3) * mm});
            skLineSegment(sketch, "E101.0.0", {"start": v(60, -40.3) * mm, "end": v(60, 40.3) * mm});
            skArc(sketch, "E101.0.1", {"start": v(60, 40.3) * mm, "mid": v(58.99, 44.68) * mm, "end": v(56.15, 48.18) * mm});
            skLineSegment(sketch, "E102", {"start": v(-15, 108) * mm, "end": v(-15, 120) * mm});
            skLineSegment(sketch, "E103", {"start": v(15, 120) * mm, "end": v(15, 108) * mm});
            skArc(sketch, "E104", {"start": v(15, 120) * mm, "mid": v(0, 135) * mm, "end": v(-15, 120) * mm});
            skCircle(sketch, "E105", {"center": v(0, 120) * mm, "radius": 6 * mm});
            skLineSegment(sketch, "E106", {"start": v(0, 120) * mm, "end": v(0, 90) * mm, "construction": true});
            skLineSegment(sketch, "E107", {"start": v(15, 108) * mm, "end": v(33, 90) * mm});
            skLineSegment(sketch, "E108", {"start": v(-15, 108) * mm, "end": v(-33, 90) * mm});
            skLineSegment(sketch, "E109", {"start": v(-80, 0) * mm, "end": v(80, 0) * mm, "construction": true});
            skLineSegment(sketch, "E110.MirrorCS", {"start": v(-15, -108) * mm, "end": v(-15, -120) * mm});
            skLineSegment(sketch, "E111.MirrorCS", {"start": v(15, -120) * mm, "end": v(15, -108) * mm});
            skArc(sketch, "E112.MirrorCS", {"start": v(15, -120) * mm, "mid": v(0, -135) * mm, "end": v(-15, -120) * mm});
            skCircle(sketch, "E113.MirrorC", {"center": v(0, -120) * mm, "radius": 6 * mm});
            skLineSegment(sketch, "E114.MirrorCS", {"start": v(0, -120) * mm, "end": v(0, -90) * mm, "construction": true});
            skLineSegment(sketch, "E115.MirrorCS", {"start": v(-15, -108) * mm, "end": v(-33, -90) * mm});
            skLineSegment(sketch, "E116.MirrorCS", {"start": v(15, -108) * mm, "end": v(33, -90) * mm});
            skSolve(sketch);
        }
        {
            var Q0;
            Q0 = qSketchRegion(id + "F16", true);
            var Q1;
            Q1=makeQuery(id+"F2.opExtrude","CAP_FACE",FACE,{"disambiguationData":[OSD([sQuery(id+"F0.wireOp",EDGE,"E12"),sQuery(id+"F0.wireOp",EDGE,"E13"),sQuery(id+"F0.wireOp",EDGE,"E14"),sQuery(id+"F0.wireOp",EDGE,"E15"),sQuery(id+"F0.wireOp",EDGE,"E17.filletArc"),sQuery(id+"F0.wireOp",EDGE,"E18.filletArc"),sQuery(id+"F0.wireOp",EDGE,"E19.filletArc"),sQuery(id+"F0.wireOp",EDGE,"E20.filletArc"),sQuery(id+"F0.wireOp",EDGE,"E25.0"),sQuery(id+"F0.wireOp",EDGE,"E25.1"),sQuery(id+"F0.wireOp",EDGE,"E25.2"),sQuery(id+"F0.wireOp",EDGE,"E25.3"),sQuery(id+"F0.wireOp",EDGE,"E25.4"),sQuery(id+"F0.wireOp",EDGE,"E25.5"),sQuery(id+"F0.wireOp",EDGE,"E25.6"),sQuery(id+"F0.wireOp",EDGE,"E25.7")])],"isStart":false});
            extrude(context, id + "F17", {"entities" : qUnion([Q0]), "endBound" : BoundingType.UP_TO_SURFACE, "endBoundEntityFace" : qUnion([Q1]), "depth" : 25 * mm});
        }
    });
